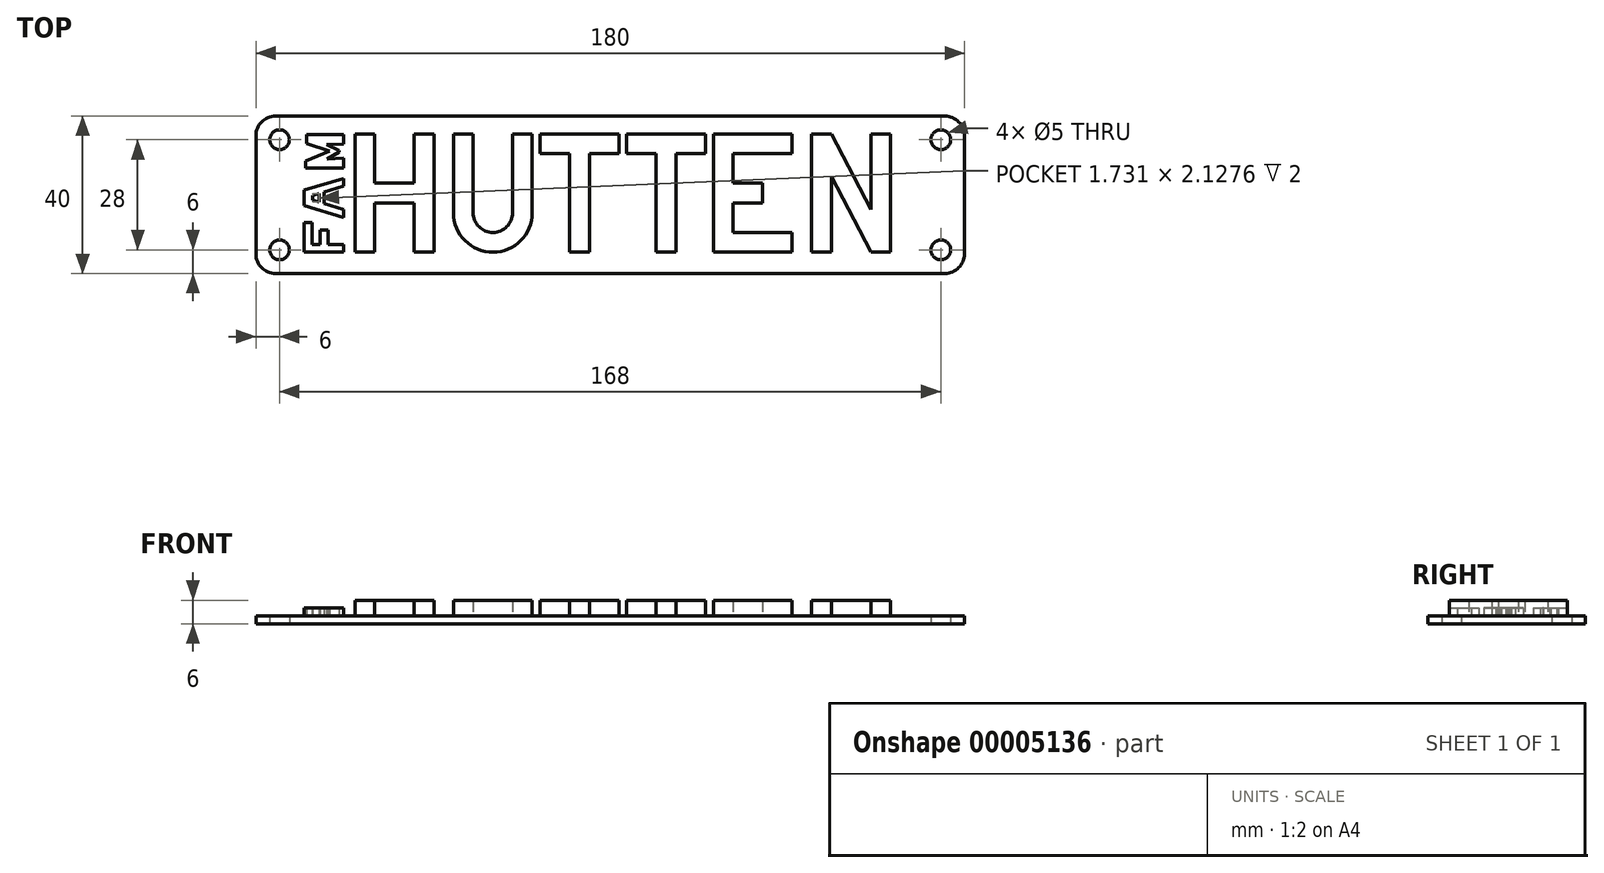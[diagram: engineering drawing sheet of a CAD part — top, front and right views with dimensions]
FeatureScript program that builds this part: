
annotation { "Feature Type Name" : "Feature", "Feature Type Description" : "" }
export const myFeature = defineFeature(function(context is Context, id is Id, definition is map)
    precondition{}
    {
        {
            var Q0;
            Q0=qCreatedBy(makeId("Top.planeOp"),FACE);
            var sketch = newSketch(context, id + "F0", { "sketchPlane" : qUnion([Q0])});
            skLineSegment(sketch, "E0.bottom", {"start": v(-85, 20) * mm, "end": v(85, 20) * mm});
            skLineSegment(sketch, "E0.top", {"start": v(-85, -20) * mm, "end": v(85, -20) * mm});
            skLineSegment(sketch, "E0.left", {"start": v(-90, 15) * mm, "end": v(-90, -15) * mm});
            skLineSegment(sketch, "E0.right", {"start": v(90, 15) * mm, "end": v(90, -15) * mm});
            skLineSegment(sketch, "E1", {"start": v(-90, 20) * mm, "end": v(90, -20) * mm, "construction": true});
            skLineSegment(sketch, "E2.bottom", {"start": v(-84, 14) * mm, "end": v(84, 14) * mm, "construction": true});
            skLineSegment(sketch, "E2.top", {"start": v(-84, -14) * mm, "end": v(84, -14) * mm, "construction": true});
            skLineSegment(sketch, "E2.left", {"start": v(-84, 14) * mm, "end": v(-84, -14) * mm, "construction": true});
            skLineSegment(sketch, "E2.right", {"start": v(84, 14) * mm, "end": v(84, -14) * mm, "construction": true});
            skCircle(sketch, "E3", {"center": v(-84, 14) * mm, "radius": 2.5 * mm});
            skCircle(sketch, "E4", {"center": v(84, 14) * mm, "radius": 2.5 * mm});
            skCircle(sketch, "E5", {"center": v(84, -14) * mm, "radius": 2.5 * mm});
            skCircle(sketch, "E6", {"center": v(-84, -14) * mm, "radius": 2.5 * mm});
            skLineSegment(sketch, "E7", {"start": v(0, 14) * mm, "end": v(0, 20) * mm, "construction": true});
            skLineSegment(sketch, "E8", {"start": v(84, 0) * mm, "end": v(90, 0) * mm, "construction": true});
            skPoint(sketch, "E9.visualSharp", {"position": v(-90, 20) * mm});
            skArc(sketch, "E9.filletArc", {"start": v(-85, 20) * mm, "mid": v(-88.54, 18.54) * mm, "end": v(-90, 15) * mm});
            skPoint(sketch, "E10.visualSharp", {"position": v(-90, -20) * mm});
            skArc(sketch, "E10.filletArc", {"start": v(-90, -15) * mm, "mid": v(-88.54, -18.54) * mm, "end": v(-85, -20) * mm});
            skPoint(sketch, "E11.visualSharp", {"position": v(90, -20) * mm});
            skArc(sketch, "E11.filletArc", {"start": v(85, -20) * mm, "mid": v(88.54, -18.54) * mm, "end": v(90, -15) * mm});
            skPoint(sketch, "E12.visualSharp", {"position": v(90, 20) * mm});
            skArc(sketch, "E12.filletArc", {"start": v(90, 15) * mm, "mid": v(88.54, 18.54) * mm, "end": v(85, 20) * mm});
            skSolve(sketch);
        }
        {
            var Q0;
            Q0=makeQuery(id+"F0.imprint","IMPRINT",FACE,{"disambiguationData":[TD([[makeQuery(id+"F0.imprint","IMPRINT",EDGE,{"derivedFrom":sQuery(id+"F0.wireOp",EDGE,"E0.bottom")}),-1.0]])]});
            extrude(context, id + "F1", {"entities" : qUnion([Q0]), "depth" : 2 * mm});
        }
        {
            var Q0;
            Q0=makeQuery(id+"F1.opExtrude","CAP_FACE",FACE,{"disambiguationData":[OSD([sQuery(id+"F0.wireOp",EDGE,"E0.bottom"),sQuery(id+"F0.wireOp",EDGE,"E0.top"),sQuery(id+"F0.wireOp",EDGE,"E0.left"),sQuery(id+"F0.wireOp",EDGE,"E0.right"),sQuery(id+"F0.wireOp",EDGE,"E3"),sQuery(id+"F0.wireOp",EDGE,"E4"),sQuery(id+"F0.wireOp",EDGE,"E5"),sQuery(id+"F0.wireOp",EDGE,"E6"),sQuery(id+"F0.wireOp",EDGE,"E9.filletArc"),sQuery(id+"F0.wireOp",EDGE,"E10.filletArc"),sQuery(id+"F0.wireOp",EDGE,"E11.filletArc"),sQuery(id+"F0.wireOp",EDGE,"E12.filletArc")])],"isStart":false});
            var sketch = newSketch(context, id + "F2", { "sketchPlane" : qUnion([Q0])});
            skLineSegment(sketch, "E13.bottom", {"start": v(-59.8, 15.43) * mm, "end": v(-64.8, 15.43) * mm});
            skLineSegment(sketch, "E13.top", {"start": v(-59.8, -14.57) * mm, "end": v(-64.8, -14.57) * mm});
            skLineSegment(sketch, "E13.left", {"start": v(-59.8, 15.43) * mm, "end": v(-59.8, 2.93) * mm});
            skLineSegment(sketch, "E13.right", {"start": v(-64.8, 15.43) * mm, "end": v(-64.8, -14.57) * mm});
            skLineSegment(sketch, "E14.bottom", {"start": v(-49.8, 15.43) * mm, "end": v(-44.8, 15.43) * mm});
            skLineSegment(sketch, "E14.top", {"start": v(-49.8, -14.57) * mm, "end": v(-44.8, -14.57) * mm});
            skLineSegment(sketch, "E14.left", {"start": v(-49.8, 15.43) * mm, "end": v(-49.8, 2.93) * mm});
            skLineSegment(sketch, "E14.right", {"start": v(-44.8, 15.43) * mm, "end": v(-44.8, -14.57) * mm});
            skLineSegment(sketch, "E15.bottom", {"start": v(-59.8, 2.93) * mm, "end": v(-49.8, 2.93) * mm});
            skLineSegment(sketch, "E15.top", {"start": v(-59.8, -2.07) * mm, "end": v(-49.8, -2.07) * mm});
            skLineSegment(sketch, "E15.left", {"start": v(-59.8, 2.93) * mm, "end": v(-59.8, -2.07) * mm, "construction": true});
            skLineSegment(sketch, "E15.right", {"start": v(-49.8, 2.93) * mm, "end": v(-49.8, -2.07) * mm, "construction": true});
            skLineSegment(sketch, "E16.bottom", {"start": v(-34.8, 15.43) * mm, "end": v(-39.8, 15.43) * mm});
            skLineSegment(sketch, "E16.top", {"start": v(-34.8, -4.57) * mm, "end": v(-39.8, -4.57) * mm, "construction": true});
            skLineSegment(sketch, "E16.left", {"start": v(-34.8, 15.43) * mm, "end": v(-34.8, -4.57) * mm});
            skLineSegment(sketch, "E16.right", {"start": v(-39.8, 15.43) * mm, "end": v(-39.8, -4.57) * mm});
            skLineSegment(sketch, "E17.bottom", {"start": v(-19.8, 15.43) * mm, "end": v(-24.8, 15.43) * mm});
            skLineSegment(sketch, "E17.top", {"start": v(-19.8, -4.57) * mm, "end": v(-24.8, -4.57) * mm, "construction": true});
            skLineSegment(sketch, "E17.left", {"start": v(-19.8, 15.43) * mm, "end": v(-19.8, -4.57) * mm});
            skLineSegment(sketch, "E17.right", {"start": v(-24.8, 15.43) * mm, "end": v(-24.8, -4.57) * mm});
            skArc(sketch, "E18", {"start": v(-39.8, -4.57) * mm, "mid": v(-29.8, -14.57) * mm, "end": v(-19.8, -4.57) * mm});
            skArc(sketch, "E19", {"start": v(-34.8, -4.57) * mm, "mid": v(-29.8, -9.57) * mm, "end": v(-24.8, -4.57) * mm});
            skLineSegment(sketch, "E20", {"start": v(-57.17, 33.33) * mm, "end": v(20.19, 33.33) * mm, "construction": true});
            skLineSegment(sketch, "E21.trimOffspring", {"start": v(-59.8, -2.07) * mm, "end": v(-59.8, -14.57) * mm});
            skLineSegment(sketch, "E22.trimOffspring", {"start": v(-49.8, -2.07) * mm, "end": v(-49.8, -14.57) * mm});
            skPoint(sketch, "E23", {"position": v(-29.8, -14.57) * mm});
            skLineSegment(sketch, "E24.bottom", {"start": v(-17.8, 15.43) * mm, "end": v(2.2, 15.43) * mm});
            skLineSegment(sketch, "E24.top", {"start": v(-17.8, 10.43) * mm, "end": v(2.2, 10.43) * mm});
            skLineSegment(sketch, "E24.left", {"start": v(-17.8, 15.43) * mm, "end": v(-17.8, 10.43) * mm});
            skLineSegment(sketch, "E24.right", {"start": v(2.2, 15.43) * mm, "end": v(2.2, 10.43) * mm});
            skLineSegment(sketch, "E25.bottom", {"start": v(-5.3, 10.43) * mm, "end": v(-10.3, 10.43) * mm, "construction": true});
            skLineSegment(sketch, "E25.top", {"start": v(-5.3, -14.57) * mm, "end": v(-10.3, -14.57) * mm});
            skLineSegment(sketch, "E25.left", {"start": v(-10.3, 10.43) * mm, "end": v(-10.3, -14.57) * mm});
            skLineSegment(sketch, "E25.right", {"start": v(-5.3, 10.43) * mm, "end": v(-5.3, -14.57) * mm});
            skPoint(sketch, "E26", {"position": v(-7.8, 10.43) * mm});
            skLineSegment(sketch, "E27.bottom", {"start": v(4.2, 15.43) * mm, "end": v(24.2, 15.43) * mm});
            skLineSegment(sketch, "E27.top", {"start": v(4.2, 10.43) * mm, "end": v(24.2, 10.43) * mm});
            skLineSegment(sketch, "E27.left", {"start": v(4.2, 15.43) * mm, "end": v(4.2, 10.43) * mm});
            skLineSegment(sketch, "E27.right", {"start": v(24.2, 15.43) * mm, "end": v(24.2, 10.43) * mm});
            skLineSegment(sketch, "E28.bottom", {"start": v(16.7, 10.43) * mm, "end": v(11.7, 10.43) * mm, "construction": true});
            skLineSegment(sketch, "E28.top", {"start": v(16.7, -14.57) * mm, "end": v(11.7, -14.57) * mm});
            skLineSegment(sketch, "E28.left", {"start": v(11.7, 10.43) * mm, "end": v(11.7, -14.57) * mm});
            skLineSegment(sketch, "E28.right", {"start": v(16.7, 10.43) * mm, "end": v(16.7, -14.57) * mm});
            skPoint(sketch, "E29", {"position": v(14.2, 10.43) * mm});
            skLineSegment(sketch, "E30.bottom", {"start": v(46.2, 15.43) * mm, "end": v(31.2, 15.43) * mm});
            skLineSegment(sketch, "E30.top", {"start": v(46.2, 10.43) * mm, "end": v(31.2, 10.43) * mm});
            skLineSegment(sketch, "E30.left", {"start": v(46.2, 15.43) * mm, "end": v(46.2, 10.43) * mm});
            skLineSegment(sketch, "E30.right", {"start": v(31.2, 15.43) * mm, "end": v(31.2, 10.43) * mm, "construction": true});
            skLineSegment(sketch, "E31.bottom", {"start": v(31.2, 15.43) * mm, "end": v(26.2, 15.43) * mm});
            skLineSegment(sketch, "E31.top", {"start": v(31.2, -14.57) * mm, "end": v(26.2, -14.57) * mm});
            skLineSegment(sketch, "E31.left", {"start": v(31.2, 10.43) * mm, "end": v(31.2, -9.57) * mm});
            skLineSegment(sketch, "E31.right", {"start": v(26.2, 15.43) * mm, "end": v(26.2, -14.57) * mm});
            skLineSegment(sketch, "E32.bottom", {"start": v(31.2, -9.57) * mm, "end": v(46.2, -9.57) * mm});
            skLineSegment(sketch, "E32.top", {"start": v(31.2, -14.57) * mm, "end": v(46.2, -14.57) * mm});
            skLineSegment(sketch, "E32.left", {"start": v(31.2, -9.57) * mm, "end": v(31.2, -14.57) * mm, "construction": true});
            skLineSegment(sketch, "E32.right", {"start": v(46.2, -9.57) * mm, "end": v(46.2, -14.57) * mm});
            skLineSegment(sketch, "E33.bottom", {"start": v(31.2, 2.93) * mm, "end": v(38.7, 2.93) * mm});
            skLineSegment(sketch, "E33.top", {"start": v(31.2, -2.07) * mm, "end": v(38.7, -2.07) * mm});
            skLineSegment(sketch, "E33.left", {"start": v(31.2, 2.93) * mm, "end": v(31.2, -2.07) * mm, "construction": true});
            skLineSegment(sketch, "E33.right", {"start": v(38.7, 2.93) * mm, "end": v(38.7, -2.07) * mm});
            skPoint(sketch, "E34", {"position": v(31.2, 0.43) * mm});
            skLineSegment(sketch, "E35.bottom", {"start": v(56.2, 15.43) * mm, "end": v(51.2, 15.43) * mm});
            skLineSegment(sketch, "E35.top", {"start": v(56.2, -14.57) * mm, "end": v(51.2, -14.57) * mm});
            skLineSegment(sketch, "E35.left", {"start": v(56.2, 4.61) * mm, "end": v(56.2, -14.57) * mm});
            skLineSegment(sketch, "E35.right", {"start": v(51.2, 15.43) * mm, "end": v(51.2, -14.57) * mm});
            skLineSegment(sketch, "E36.bottom", {"start": v(71.2, 15.43) * mm, "end": v(66.2, 15.43) * mm});
            skLineSegment(sketch, "E36.top", {"start": v(71.2, -14.57) * mm, "end": v(66.2, -14.57) * mm});
            skLineSegment(sketch, "E36.left", {"start": v(71.2, 15.43) * mm, "end": v(71.2, -14.57) * mm});
            skLineSegment(sketch, "E36.right", {"start": v(66.2, 15.43) * mm, "end": v(66.2, -3.76) * mm});
            skLineSegment(sketch, "E37", {"start": v(56.2, 15.43) * mm, "end": v(66.2, -3.76) * mm});
            skLineSegment(sketch, "E38", {"start": v(66.2, -14.57) * mm, "end": v(56.2, 4.61) * mm});
            skLineSegment(sketch, "E39", {"start": v(-44.8, 15.43) * mm, "end": v(-39.8, 15.43) * mm, "construction": true});
            skLineSegment(sketch, "E40", {"start": v(46.2, 15.43) * mm, "end": v(51.2, 15.43) * mm, "construction": true});
            skLineSegment(sketch, "E41", {"start": v(-64.8, -14.57) * mm, "end": v(-44.8, -14.57) * mm, "construction": true});
            skLineSegment(sketch, "E42", {"start": v(-39.8, 15.43) * mm, "end": v(-19.8, 15.43) * mm, "construction": true});
            skLineSegment(sketch, "E43", {"start": v(46.2, -14.57) * mm, "end": v(26.2, -14.57) * mm, "construction": true});
            skLineSegment(sketch, "E44", {"start": v(51.2, -14.57) * mm, "end": v(71.2, -14.57) * mm, "construction": true});
            skPoint(sketch, "E45", {"position": v(-49.8, 0.43) * mm});
            skLineSegment(sketch, "E46", {"start": v(-49.8, 0.43) * mm, "end": v(-44.8, 0.43) * mm, "construction": true});
            skPoint(sketch, "E47", {"position": v(0, 0) * mm});
            skLineSegment(sketch, "E48", {"start": v(38.7, 2.93) * mm, "end": v(38.7, 10.43) * mm, "construction": true});
            skLineSegment(sketch, "E49", {"start": v(58.82, -0.4) * mm, "end": v(63.25, 1.9) * mm, "construction": true});
            skLineSegment(sketch, "E50", {"start": v(-19.8, 15.43) * mm, "end": v(-17.8, 15.43) * mm, "construction": true});
            skLineSegment(sketch, "E51", {"start": v(2.2, 15.43) * mm, "end": v(4.2, 15.43) * mm, "construction": true});
            skLineSegment(sketch, "E52", {"start": v(24.2, 15.43) * mm, "end": v(26.2, 15.43) * mm, "construction": true});
            skSolve(sketch);
        }
        {
            var Q0;
            Q0=makeQuery(id+"F2.imprint","IMPRINT",FACE,{"disambiguationData":[TD([[makeQuery(id+"F2.imprint","IMPRINT",EDGE,{"derivedFrom":sQuery(id+"F2.wireOp",EDGE,"E13.bottom")}),1.0]])]});
            var Q1;
            Q1=makeQuery(id+"F2.imprint","IMPRINT",FACE,{"disambiguationData":[TD([[makeQuery(id+"F2.imprint","IMPRINT",EDGE,{"derivedFrom":sQuery(id+"F2.wireOp",EDGE,"E16.bottom")}),1.0]])]});
            var Q2;
            Q2=makeQuery(id+"F2.imprint","IMPRINT",FACE,{"disambiguationData":[TD([[makeQuery(id+"F2.imprint","IMPRINT",EDGE,{"derivedFrom":sQuery(id+"F2.wireOp",EDGE,"E25.top")}),-1.0]])]});
            var Q3;
            Q3=makeQuery(id+"F2.imprint","IMPRINT",FACE,{"disambiguationData":[TD([[makeQuery(id+"F2.imprint","IMPRINT",EDGE,{"derivedFrom":sQuery(id+"F2.wireOp",EDGE,"E28.top")}),-1.0]])]});
            var Q4;
            Q4=makeQuery(id+"F2.imprint","IMPRINT",FACE,{"disambiguationData":[TD([[makeQuery(id+"F2.imprint","IMPRINT",EDGE,{"derivedFrom":sQuery(id+"F2.wireOp",EDGE,"E27.bottom")}),-1.0]])]});
            var Q5;
            Q5=makeQuery(id+"F2.imprint","IMPRINT",FACE,{"disambiguationData":[TD([[makeQuery(id+"F2.imprint","IMPRINT",EDGE,{"derivedFrom":sQuery(id+"F2.wireOp",EDGE,"E24.bottom")}),-1.0]])]});
            var Q6;
            Q6=makeQuery(id+"F2.imprint","IMPRINT",FACE,{"disambiguationData":[TD([[makeQuery(id+"F2.imprint","IMPRINT",EDGE,{"derivedFrom":sQuery(id+"F2.wireOp",EDGE,"E30.bottom")}),1.0]])]});
            var Q7;
            {var subQ1=sQuery(id+"F2.wireOp",EDGE,"E33.bottom");Q7=makeQuery(id+"F2.imprint","IMPRINT",FACE,{"disambiguationData":[TD([[makeQuery(id+"F2.imprint","IMPRINT",EDGE,{"derivedFrom":subQ1}),-1.0]])]});}
            var Q8;
            Q8=makeQuery(id+"F2.imprint","IMPRINT",FACE,{"disambiguationData":[TD([[makeQuery(id+"F2.imprint","IMPRINT",EDGE,{"derivedFrom":sQuery(id+"F2.wireOp",EDGE,"E35.bottom")}),1.0]])]});
            extrude(context, id + "F3", {"entities" : qUnion([Q0, Q1, Q2, Q3, Q4, Q5, Q6, Q7, Q8]), "operationType" : NewBodyOperationType.ADD, "depth" : 4 * mm});
        }
        {
            var Q0;
            Q0=makeQuery(id+"F1.opExtrude","CAP_FACE",FACE,{"disambiguationData":[OSD([sQuery(id+"F0.wireOp",EDGE,"E0.bottom"),sQuery(id+"F0.wireOp",EDGE,"E0.top"),sQuery(id+"F0.wireOp",EDGE,"E0.left"),sQuery(id+"F0.wireOp",EDGE,"E0.right"),sQuery(id+"F0.wireOp",EDGE,"E3"),sQuery(id+"F0.wireOp",EDGE,"E4"),sQuery(id+"F0.wireOp",EDGE,"E5"),sQuery(id+"F0.wireOp",EDGE,"E6"),sQuery(id+"F0.wireOp",EDGE,"E9.filletArc"),sQuery(id+"F0.wireOp",EDGE,"E10.filletArc"),sQuery(id+"F0.wireOp",EDGE,"E11.filletArc"),sQuery(id+"F0.wireOp",EDGE,"E12.filletArc")])],"isStart":false});
            var sketch = newSketch(context, id + "F4", { "sketchPlane" : qUnion([Q0])});
            skLineSegment(sketch, "E53.bottom", {"start": v(-67.73, -14.57) * mm, "end": v(-77.73, -14.57) * mm});
            skLineSegment(sketch, "E53.top", {"start": v(-67.73, -12.57) * mm, "end": v(-71.7, -12.57) * mm});
            skLineSegment(sketch, "E53.left", {"start": v(-67.73, -14.57) * mm, "end": v(-67.73, -12.57) * mm});
            skLineSegment(sketch, "E53.right", {"start": v(-77.73, -14.57) * mm, "end": v(-77.73, -12.57) * mm});
            skLineSegment(sketch, "E54.top", {"start": v(-77.73, -7.07) * mm, "end": v(-75.73, -7.07) * mm});
            skLineSegment(sketch, "E54.left", {"start": v(-77.73, -12.57) * mm, "end": v(-77.73, -7.07) * mm});
            skLineSegment(sketch, "E54.right", {"start": v(-75.73, -12.57) * mm, "end": v(-75.73, -7.07) * mm});
            skLineSegment(sketch, "E55.top", {"start": v(-73.7, -8.98) * mm, "end": v(-71.7, -8.98) * mm});
            skLineSegment(sketch, "E55.left", {"start": v(-73.7, -12.57) * mm, "end": v(-73.7, -8.98) * mm});
            skLineSegment(sketch, "E55.right", {"start": v(-71.7, -12.57) * mm, "end": v(-71.7, -8.98) * mm});
            skLineSegment(sketch, "E56.trimOffspring", {"start": v(-73.7, -12.57) * mm, "end": v(-75.73, -12.57) * mm});
            skLineSegment(sketch, "E57.bottom", {"start": v(-77.73, -14.57) * mm, "end": v(-67.73, -14.57) * mm, "construction": true});
            skLineSegment(sketch, "E57.top", {"start": v(-77.73, -7.07) * mm, "end": v(-67.73, -7.07) * mm, "construction": true});
            skLineSegment(sketch, "E57.left", {"start": v(-77.73, -14.57) * mm, "end": v(-77.73, -7.07) * mm, "construction": true});
            skLineSegment(sketch, "E57.right", {"start": v(-67.73, -14.57) * mm, "end": v(-67.73, -7.07) * mm, "construction": true});
            skLineSegment(sketch, "E58.bottom", {"start": v(-79.58, -5.75) * mm, "end": v(-67.73, -5.75) * mm, "construction": true});
            skLineSegment(sketch, "E58.top", {"start": v(-79.58, 4.17) * mm, "end": v(-67.73, 4.17) * mm, "construction": true});
            skLineSegment(sketch, "E58.left", {"start": v(-79.58, -5.75) * mm, "end": v(-79.58, 4.17) * mm, "construction": true});
            skLineSegment(sketch, "E58.right", {"start": v(-67.73, -5.75) * mm, "end": v(-67.73, 4.17) * mm, "construction": true});
            skLineSegment(sketch, "E59", {"start": v(-67.73, -5.75) * mm, "end": v(-77.73, -2.79) * mm});
            skLineSegment(sketch, "E60", {"start": v(-77.73, -2.79) * mm, "end": v(-77.73, 1.21) * mm});
            skLineSegment(sketch, "E61", {"start": v(-77.73, 1.21) * mm, "end": v(-67.73, 4.17) * mm});
            skLineSegment(sketch, "E62", {"start": v(-67.73, 4.17) * mm, "end": v(-67.73, 2.17) * mm});
            skLineSegment(sketch, "E63", {"start": v(-67.73, 2.17) * mm, "end": v(-72.73, 0.7) * mm});
            skLineSegment(sketch, "E64", {"start": v(-72.73, 0.7) * mm, "end": v(-72.73, -2.27) * mm});
            skLineSegment(sketch, "E65", {"start": v(-72.73, -2.27) * mm, "end": v(-67.73, -3.75) * mm});
            skLineSegment(sketch, "E66", {"start": v(-67.73, -3.75) * mm, "end": v(-67.73, -5.75) * mm});
            skLineSegment(sketch, "E67", {"start": v(-72.73, -0.79) * mm, "end": v(-67.73, -0.79) * mm, "construction": true});
            skLineSegment(sketch, "E68", {"start": v(-72.73, -0.79) * mm, "end": v(-73.91, -0.79) * mm, "construction": true});
            skLineSegment(sketch, "E69", {"start": v(-79.58, -0.79) * mm, "end": v(-77.73, -0.79) * mm, "construction": true});
            skLineSegment(sketch, "E70", {"start": v(-73.91, -1.85) * mm, "end": v(-75.65, -1.34) * mm});
            skLineSegment(sketch, "E71", {"start": v(-75.65, -1.34) * mm, "end": v(-75.65, -0.23) * mm});
            skLineSegment(sketch, "E72", {"start": v(-75.65, -0.23) * mm, "end": v(-73.91, 0.28) * mm});
            skLineSegment(sketch, "E73", {"start": v(-73.91, 0.28) * mm, "end": v(-73.91, -1.85) * mm});
            skLineSegment(sketch, "E74", {"start": v(-73.91, -0.79) * mm, "end": v(-75.65, -0.79) * mm, "construction": true});
            skLineSegment(sketch, "E75.bottom", {"start": v(-67.73, 6.82) * mm, "end": v(-79.29, 6.82) * mm, "construction": true});
            skLineSegment(sketch, "E75.top", {"start": v(-67.73, 15.32) * mm, "end": v(-79.29, 15.32) * mm, "construction": true});
            skLineSegment(sketch, "E75.left", {"start": v(-67.73, 6.82) * mm, "end": v(-67.73, 15.32) * mm, "construction": true});
            skLineSegment(sketch, "E75.right", {"start": v(-79.29, 6.82) * mm, "end": v(-79.29, 15.32) * mm, "construction": true});
            skLineSegment(sketch, "E76", {"start": v(-67.73, 6.82) * mm, "end": v(-77.36, 6.82) * mm});
            skLineSegment(sketch, "E77", {"start": v(-77.36, 6.82) * mm, "end": v(-77.36, 8.52) * mm});
            skLineSegment(sketch, "E78", {"start": v(-77.36, 8.52) * mm, "end": v(-71.34, 11.07) * mm});
            skLineSegment(sketch, "E79", {"start": v(-71.34, 11.07) * mm, "end": v(-77.15, 13.07) * mm});
            skLineSegment(sketch, "E80", {"start": v(-77.15, 13.07) * mm, "end": v(-77.15, 15.32) * mm});
            skLineSegment(sketch, "E81", {"start": v(-77.15, 15.32) * mm, "end": v(-67.73, 15.32) * mm});
            skLineSegment(sketch, "E82", {"start": v(-67.73, 6.82) * mm, "end": v(-67.73, 9.3) * mm});
            skLineSegment(sketch, "E83", {"start": v(-67.73, 9.3) * mm, "end": v(-71.97, 9.14) * mm});
            skLineSegment(sketch, "E84", {"start": v(-71.97, 9.14) * mm, "end": v(-68.9, 10.92) * mm});
            skLineSegment(sketch, "E85", {"start": v(-68.9, 10.92) * mm, "end": v(-68.9, 11.22) * mm});
            skLineSegment(sketch, "E86", {"start": v(-68.9, 11.22) * mm, "end": v(-72, 12.7) * mm});
            skLineSegment(sketch, "E87", {"start": v(-72, 12.7) * mm, "end": v(-67.73, 12.85) * mm});
            skLineSegment(sketch, "E88", {"start": v(-67.73, 12.85) * mm, "end": v(-67.73, 15.32) * mm});
            skLineSegment(sketch, "E89", {"start": v(-68.9, 11.07) * mm, "end": v(-67.73, 11.07) * mm, "construction": true});
            skSolve(sketch);
        }
        {
            var Q0;
            Q0=makeQuery(id+"F4.imprint","IMPRINT",FACE,{"disambiguationData":[TD([[makeQuery(id+"F4.imprint","IMPRINT",EDGE,{"derivedFrom":sQuery(id+"F4.wireOp",EDGE,"E53.bottom")}),-1.0]])]});
            var Q1;
            Q1=makeQuery(id+"F4.imprint","IMPRINT",FACE,{"disambiguationData":[TD([[makeQuery(id+"F4.imprint","IMPRINT",EDGE,{"derivedFrom":sQuery(id+"F4.wireOp",EDGE,"E59")}),-1.0]])]});
            var Q2;
            Q2=makeQuery(id+"F4.imprint","IMPRINT",FACE,{"disambiguationData":[TD([[makeQuery(id+"F4.imprint","IMPRINT",EDGE,{"derivedFrom":sQuery(id+"F4.wireOp",EDGE,"E76")}),-1.0]])]});
            extrude(context, id + "F5", {"entities" : qUnion([Q0, Q1, Q2]), "operationType" : NewBodyOperationType.ADD, "depth" : 2 * mm});
        }
    });
